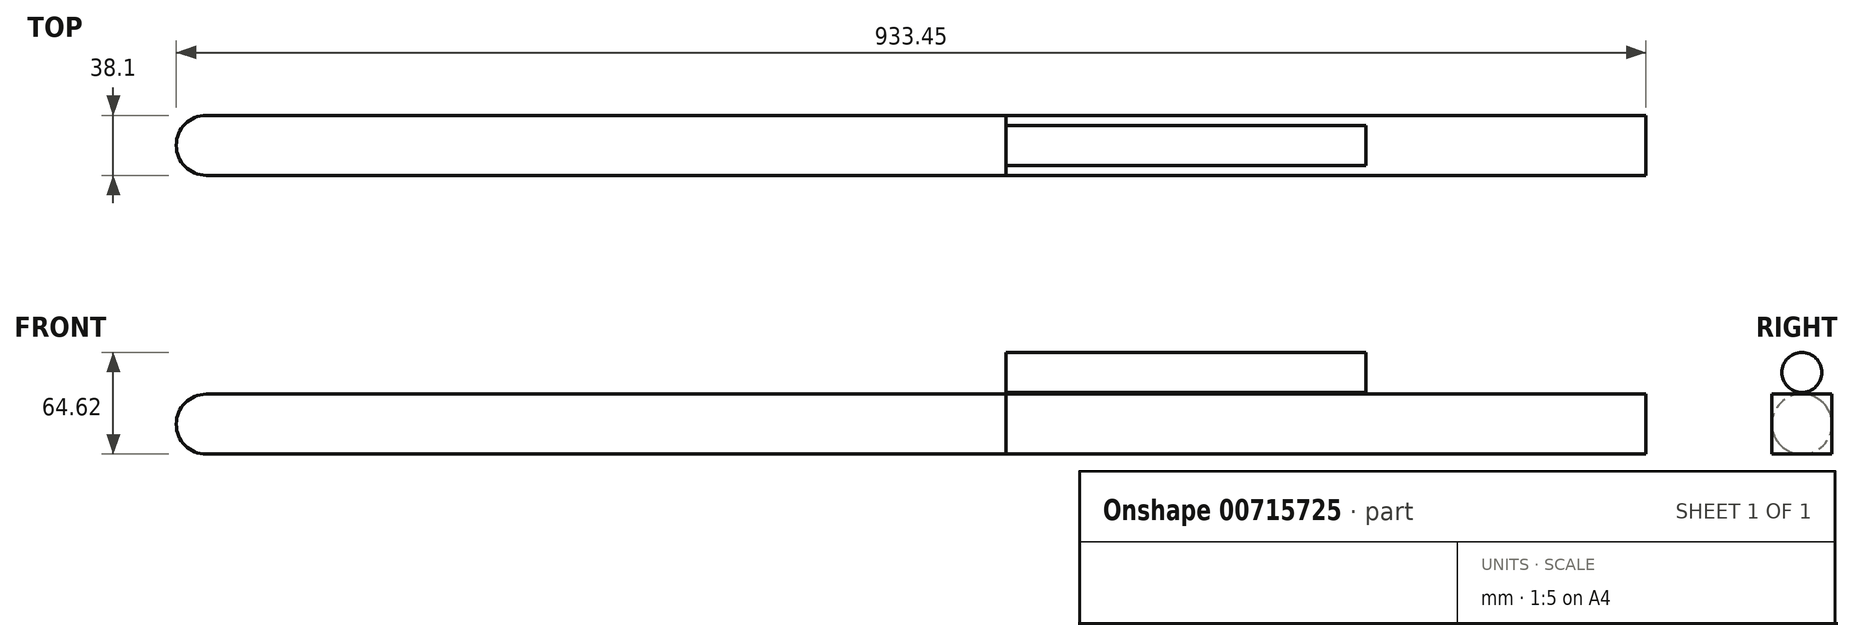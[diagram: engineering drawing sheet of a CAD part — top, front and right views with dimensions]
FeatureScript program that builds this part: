
annotation { "Feature Type Name" : "Feature", "Feature Type Description" : "" }
export const myFeature = defineFeature(function(context is Context, id is Id, definition is map)
    precondition{}
    {
        {
            var Q0;
            Q0=qCreatedBy(makeId("Right.planeOp"),FACE);
            var sketch = newSketch(context, id + "F0", { "sketchPlane" : qUnion([Q0])});
            skCircle(sketch, "E0", {"center": v(0, 0) * mm, "radius": 12.7 * mm});
            skSolve(sketch);
        }
        {
            var Q0;
            Q0=makeQuery(id+"F0.imprint","IMPRINT",FACE,{"disambiguationData":[TD([[makeQuery(id+"F0.imprint","IMPRINT",EDGE,{"derivedFrom":sQuery(id+"F0.wireOp",EDGE,"E0")}),1.0]])]});
            extrude(context, id + "F1", {"entities" : qUnion([Q0]), "depth" : 228.6 * mm, "offsetDistance" : 25.4 * mm});
        }
        {
            var Q0;
            Q0=qCreatedBy(makeId("Right.planeOp"),FACE);
            var sketch = newSketch(context, id + "F2", { "sketchPlane" : qUnion([Q0])});
            skLineSegment(sketch, "E1.bottom", {"start": v(-19.05, -51.92) * mm, "end": v(19.05, -51.92) * mm});
            skLineSegment(sketch, "E1.top", {"start": v(-19.05, -13.82) * mm, "end": v(19.05, -13.82) * mm});
            skLineSegment(sketch, "E1.left", {"start": v(-19.05, -51.92) * mm, "end": v(-19.05, -13.82) * mm});
            skLineSegment(sketch, "E1.right", {"start": v(19.05, -51.92) * mm, "end": v(19.05, -13.82) * mm});
            skPoint(sketch, "E1.middle", {"position": v(0, -32.87) * mm});
            skSolve(sketch);
        }
        {
            var Q0;
            Q0=makeQuery(id+"F2.imprint","IMPRINT",FACE,{"disambiguationData":[TD([[makeQuery(id+"F2.imprint","IMPRINT",EDGE,{"derivedFrom":sQuery(id+"F2.wireOp",EDGE,"E1.bottom")}),1.0]])]});
            extrude(context, id + "F3", {"entities" : qUnion([Q0]), "depth" : 406.4 * mm, "offsetDistance" : 25.4 * mm});
        }
        {
            var Q0;
            Q0=makeQuery(id+"F3.opExtrude","CAP_FACE",FACE,{"disambiguationData":[OSD([sQuery(id+"F2.wireOp",EDGE,"E1.bottom"),sQuery(id+"F2.wireOp",EDGE,"E1.top"),sQuery(id+"F2.wireOp",EDGE,"E1.left"),sQuery(id+"F2.wireOp",EDGE,"E1.right")])],"isStart":true});
            var sketch = newSketch(context, id + "F4", { "sketchPlane" : qUnion([Q0])});
            skCircle(sketch, "E2", {"center": v(0, -32.87) * mm, "radius": 19.05 * mm});
            skPoint(sketch, "E2.first.point", {"position": v(-19.05, -32.87) * mm});
            skPoint(sketch, "E2.second.point", {"position": v(19.05, -32.87) * mm});
            skPoint(sketch, "E2.third.point", {"position": v(0, -51.92) * mm});
            skSolve(sketch);
        }
        {
            var Q0;
            {var subQ0=sQuery(id+"F4.wireOp",EDGE,"E2");var subQ1=makeQuery(id+"F4.imprint","INTERSECT",VERTEX,{"derivedFrom":[makeQuery(id+"F3.opExtrude","CAP_EDGE",EDGE,{"disambiguationData":[OSD([sQuery(id+"F2.wireOp",EDGE,"E1.top")])],"isStart":true}),subQ0]});Q0=makeQuery(id+"F4.imprint","IMPRINT",FACE,{"disambiguationData":[TD([[makeQuery(id+"F4.imprint","IMPRINT",EDGE,{"disambiguationData":[TD([[subQ1,1.0]])],"derivedFrom":subQ0}),1.0]])]});}
            extrude(context, id + "F5", {"entities" : qUnion([Q0]), "operationType" : NewBodyOperationType.ADD, "depth" : 508 * mm, "offsetDistance" : 25.4 * mm});
        }
        {
            var Q0;
            Q0=makeQuery(id+"F5.opExtrude","CAP_FACE",FACE,{"disambiguationData":[OSD([sQuery(id+"F4.wireOp",EDGE,"E2")])],"isStart":false});
            var sketch = newSketch(context, id + "F6", { "sketchPlane" : qUnion([Q0])});
            skLineSegment(sketch, "E3", {"start": v(0, -13.82) * mm, "end": v(0, -51.92) * mm});
            skSolve(sketch);
        }
        {
            var Q0;
            {var subQ0=sQuery(id+"F6.wireOp",EDGE,"E3");Q0=makeQuery(id+"F6.imprint","IMPRINT",FACE,{"disambiguationData":[TD([[makeQuery(id+"F6.imprint","IMPRINT",EDGE,{"derivedFrom":subQ0}),1.0]])]});}
            var Q1;
            Q1=sQuery(id+"F6.wireOp",EDGE,"E3");
            revolve(context, id + "F7", {"operationType" : NewBodyOperationType.ADD, "surfaceOperationType" : NewSurfaceOperationType.NEW, "entities" : qUnion([Q0]), "axis" : qUnion([Q1]), "revolveType" : RevolveType.FULL});
        }
    });
